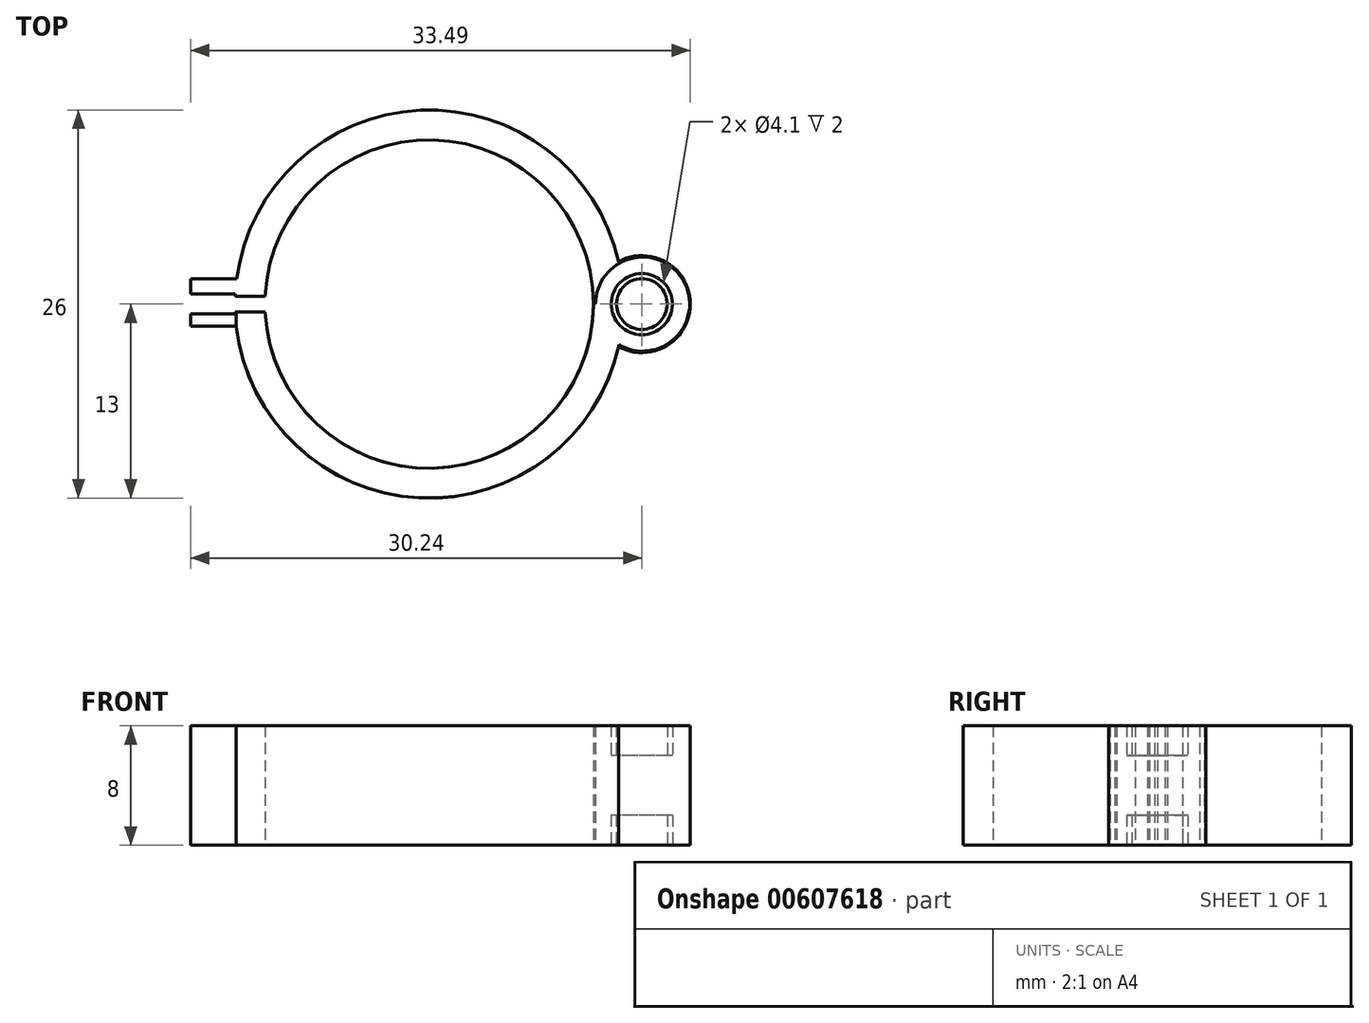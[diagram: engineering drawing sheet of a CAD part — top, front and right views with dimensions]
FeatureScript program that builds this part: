
annotation { "Feature Type Name" : "Feature", "Feature Type Description" : "" }
export const myFeature = defineFeature(function(context is Context, id is Id, definition is map)
    precondition{}
    {
        {
            var Q0;
            Q0=qCreatedBy(makeId("Top.planeOp"),FACE);
            var sketch = newSketch(context, id + "F0", { "sketchPlane" : qUnion([Q0])});
            skArc(sketch, "E0", {"start": v(11, 0) * mm, "mid": v(0, 11) * mm, "end": v(-11, 0) * mm});
            skArc(sketch, "E1", {"start": v(12.68, -2.85) * mm, "mid": v(17.5, 0) * mm, "end": v(12.68, 2.85) * mm});
            skArc(sketch, "E2", {"start": v(12.68, 2.85) * mm, "mid": v(-1.43, 12.92) * mm, "end": v(-13, 0) * mm});
            skCircle(sketch, "E3", {"center": v(14.25, 0) * mm, "radius": 1.7 * mm});
            skCircle(sketch, "E4", {"center": v(14.25, 0) * mm, "radius": 2.05 * mm});
            skCircle(sketch, "E5", {"center": v(14.25, 0) * mm, "radius": 3.25 * mm});
            skLineSegment(sketch, "E6", {"start": v(-19.7, 0) * mm, "end": v(32.54, 0) * mm, "construction": true});
            skLineSegment(sketch, "E7", {"start": v(-13, 0) * mm, "end": v(-11, 0) * mm});
            skLineSegment(sketch, "E8", {"start": v(14.23, -12.18) * mm, "end": v(14.23, 19.52) * mm, "construction": true});
            skLineSegment(sketch, "E9.bottom", {"start": v(-12.9, 1.69) * mm, "end": v(-15.96, 1.69) * mm});
            skLineSegment(sketch, "E9.top", {"start": v(-12.9, 0.67) * mm, "end": v(-15.96, 0.67) * mm});
            skLineSegment(sketch, "E9.left", {"start": v(-12.9, 1.69) * mm, "end": v(-12.9, 0.67) * mm});
            skLineSegment(sketch, "E9.right", {"start": v(-15.96, 1.69) * mm, "end": v(-15.96, 0.67) * mm});
            skSolve(sketch);
        }
        {
            var Q0;
            Q0 = qSketchRegion(id + "F0", true);
            extrude(context, id + "F1", {"entities" : qUnion([Q0]), "endBound" : BoundingType.SYMMETRIC, "depth" : 8 * mm, "offsetDistance" : 25 * mm});
        }
        {
            var Q0;
            Q0=makeQuery(id+"F0.imprint","IMPRINT",FACE,{"disambiguationData":[TD([[makeQuery(id+"F0.imprint","IMPRINT",EDGE,{"derivedFrom":sQuery(id+"F0.wireOp",EDGE,"E4")}),-1.0]])]});
            extrude(context, id + "F2", {"entities" : qUnion([Q0]), "operationType" : NewBodyOperationType.REMOVE, "endBound" : BoundingType.SYMMETRIC, "oppositeDirection" : true, "depth" : 4 * mm, "offsetDistance" : 25 * mm});
        }
        {
            var Q0;
            Q0=qCreatedBy(makeId("Top.planeOp"),FACE);
            var sketch = newSketch(context, id + "F3", { "sketchPlane" : qUnion([Q0])});
            skArc(sketch, "E10", {"start": v(-11, 0) * mm, "mid": v(0, -11) * mm, "end": v(11, 0) * mm});
            skArc(sketch, "E11", {"start": v(-13, 0) * mm, "mid": v(0, -13) * mm, "end": v(13, 0) * mm});
            skLineSegment(sketch, "E12", {"start": v(-18.45, 0) * mm, "end": v(19.72, 0) * mm, "construction": true});
            skLineSegment(sketch, "E13", {"start": v(-13, 0) * mm, "end": v(-11, 0) * mm});
            skLineSegment(sketch, "E14", {"start": v(11, 0) * mm, "end": v(13, 0) * mm});
            skCircle(sketch, "E15", {"center": v(14.3, 0) * mm, "radius": 3.15 * mm});
            skLineSegment(sketch, "E16.bottom", {"start": v(-12.91, -1.5) * mm, "end": v(-15.99, -1.5) * mm});
            skLineSegment(sketch, "E16.top", {"start": v(-12.91, -0.66) * mm, "end": v(-15.99, -0.66) * mm});
            skLineSegment(sketch, "E16.left", {"start": v(-12.91, -1.5) * mm, "end": v(-12.91, -0.66) * mm});
            skLineSegment(sketch, "E16.right", {"start": v(-15.99, -1.5) * mm, "end": v(-15.99, -0.66) * mm});
            skSolve(sketch);
        }
        {
            var Q0;
            Q0=sQuery(id+"F3.wireOp",EDGE,"E15");
            var Q1;
            Q1=sQuery(id+"F0.wireOp",EDGE,"E3");
            extrude(context, id + "F4", {"bodyType" : ToolBodyType.SURFACE, "surfaceEntities" : qUnion([Q0, Q1]), "endBound" : BoundingType.SYMMETRIC, "depth" : 4 * mm, "offsetDistance" : 25 * mm});
        }
        {
            var Q0;
            {var subQ1=sQuery(id+"F3.wireOp",EDGE,"E10");Q0=makeQuery(id+"F3.imprint","IMPRINT",FACE,{"disambiguationData":[TD([[makeQuery(id+"F3.imprint","IMPRINT",EDGE,{"derivedFrom":subQ1}),-1.0]])]});}
            extrude(context, id + "F5", {"entities" : qUnion([Q0]), "endBound" : BoundingType.SYMMETRIC, "depth" : 8 * mm, "offsetDistance" : 25 * mm});
        }
        {
            var Q0;
            Q0=qCreatedBy(makeId("Top.planeOp"),FACE);
            var sketch = newSketch(context, id + "F6", { "sketchPlane" : qUnion([Q0])});
            skLineSegment(sketch, "E17.bottom", {"start": v(-10, -0.53) * mm, "end": v(-17.84, -0.53) * mm});
            skLineSegment(sketch, "E17.top", {"start": v(-10, 0.53) * mm, "end": v(-17.84, 0.53) * mm});
            skLineSegment(sketch, "E17.left", {"start": v(-10, -0.53) * mm, "end": v(-10, 0.53) * mm});
            skLineSegment(sketch, "E17.right", {"start": v(-17.84, -0.53) * mm, "end": v(-17.84, 0.53) * mm});
            skPoint(sketch, "E17.middle", {"position": v(-13.92, 0) * mm});
            skSolve(sketch);
        }
        {
            var Q0;
            Q0 = qSketchRegion(id + "F6", true);
            extrude(context, id + "F7", {"entities" : qUnion([Q0]), "operationType" : NewBodyOperationType.REMOVE, "endBound" : BoundingType.SYMMETRIC, "oppositeDirection" : true, "depth" : 9 * mm, "offsetDistance" : 25 * mm});
        }
        {
            var Q0;
            Q0=makeQuery(id+"F0.imprint","IMPRINT",FACE,{"disambiguationData":[TD([[makeQuery(id+"F0.imprint","IMPRINT",EDGE,{"derivedFrom":sQuery(id+"F0.wireOp",EDGE,"E3")}),-1.0]])]});
            var Q1;
            Q1=sQuery(id+"F0.wireOp",EDGE,"E4");
            var Q2;
            Q2=sQuery(id+"F0.wireOp",EDGE,"E3");
            extrude(context, id + "F8", {"entities" : qUnion([Q0]), "surfaceEntities" : qUnion([Q1, Q2]), "endBound" : BoundingType.SYMMETRIC, "depth" : 4 * mm, "offsetDistance" : 25 * mm});
        }
        {
            var Q0;
            Q0=makeQuery(id+"F0.imprint","IMPRINT",FACE,{"disambiguationData":[TD([[makeQuery(id+"F0.imprint","IMPRINT",EDGE,{"derivedFrom":sQuery(id+"F0.wireOp",EDGE,"E3")}),1.0]])]});
            extrude(context, id + "F9", {"entities" : qUnion([Q0]), "operationType" : NewBodyOperationType.ADD, "endBound" : BoundingType.SYMMETRIC, "depth" : 8 * mm, "offsetDistance" : 25 * mm});
        }
        {
            var Q0;
            Q0=qCreatedBy(makeId("Top.planeOp"),FACE);
            var sketch = newSketch(context, id + "F10", { "sketchPlane" : qUnion([Q0])});
            skLineSegment(sketch, "E18.bottom", {"start": v(10.62, 0.17) * mm, "end": v(12.2, 0.17) * mm});
            skLineSegment(sketch, "E18.top", {"start": v(10.62, -0.17) * mm, "end": v(12.2, -0.17) * mm});
            skLineSegment(sketch, "E18.left", {"start": v(10.62, 0.17) * mm, "end": v(10.62, -0.17) * mm});
            skLineSegment(sketch, "E18.right", {"start": v(12.2, 0.17) * mm, "end": v(12.2, -0.17) * mm});
            skPoint(sketch, "E18.middle", {"position": v(11.4, 0) * mm});
            skSolve(sketch);
        }
        {
            var Q0;
            Q0 = qSketchRegion(id + "F10", true);
            extrude(context, id + "F11", {"entities" : qUnion([Q0]), "operationType" : NewBodyOperationType.REMOVE, "endBound" : BoundingType.SYMMETRIC, "oppositeDirection" : true, "depth" : 8 * mm, "offsetDistance" : 25 * mm});
        }
        {
            var Q0;
            Q0 = qSketchRegion(id + "F0", true);
            extrude(context, id + "F12", {"entities" : qUnion([Q0]), "operationType" : NewBodyOperationType.ADD, "endBound" : BoundingType.SYMMETRIC, "depth" : 8 * mm, "offsetDistance" : 25 * mm});
        }
        {
            var Q0;
            Q0 = qSketchRegion(id + "F3", true);
            extrude(context, id + "F13", {"entities" : qUnion([Q0]), "endBound" : BoundingType.SYMMETRIC, "depth" : 8 * mm, "offsetDistance" : 25 * mm});
        }
        {
            var Q0;
            Q0 = qSketchRegion(id + "F6", true);
            extrude(context, id + "F14", {"entities" : qUnion([Q0]), "operationType" : NewBodyOperationType.REMOVE, "endBound" : BoundingType.SYMMETRIC, "oppositeDirection" : true, "depth" : 8 * mm, "offsetDistance" : 25 * mm});
        }
    });
